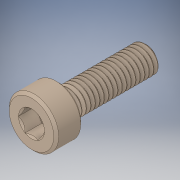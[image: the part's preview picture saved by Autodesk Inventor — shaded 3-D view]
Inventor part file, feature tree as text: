
AUTODESK INVENTOR PART (.ipt)
format: ipt  version: 2019 (Build 230136000, 136)  size: 579,584 bytes
history: mixed  units: mm
features: chamfer x1, imported_body x1
ambient origin geometry x8: Origin, YZ Plane, XZ Plane, XY Plane, X Axis, Y Axis, Z Axis, Center Point
bodies: Solid1 (imported_parasolid)
feature tree (2):
  chamfer  "Chamfer1"  [1 undecoded]
  imported_body  NMx_Import_Brep_tag  [imported B-rep: ~3 faces, bbox_mm=None]
note: 1 required parameter value undecoded (feature->parameter linkage not recoverable at this tier; creation-order binding heuristic only, values carry confidence <= 0.55)
